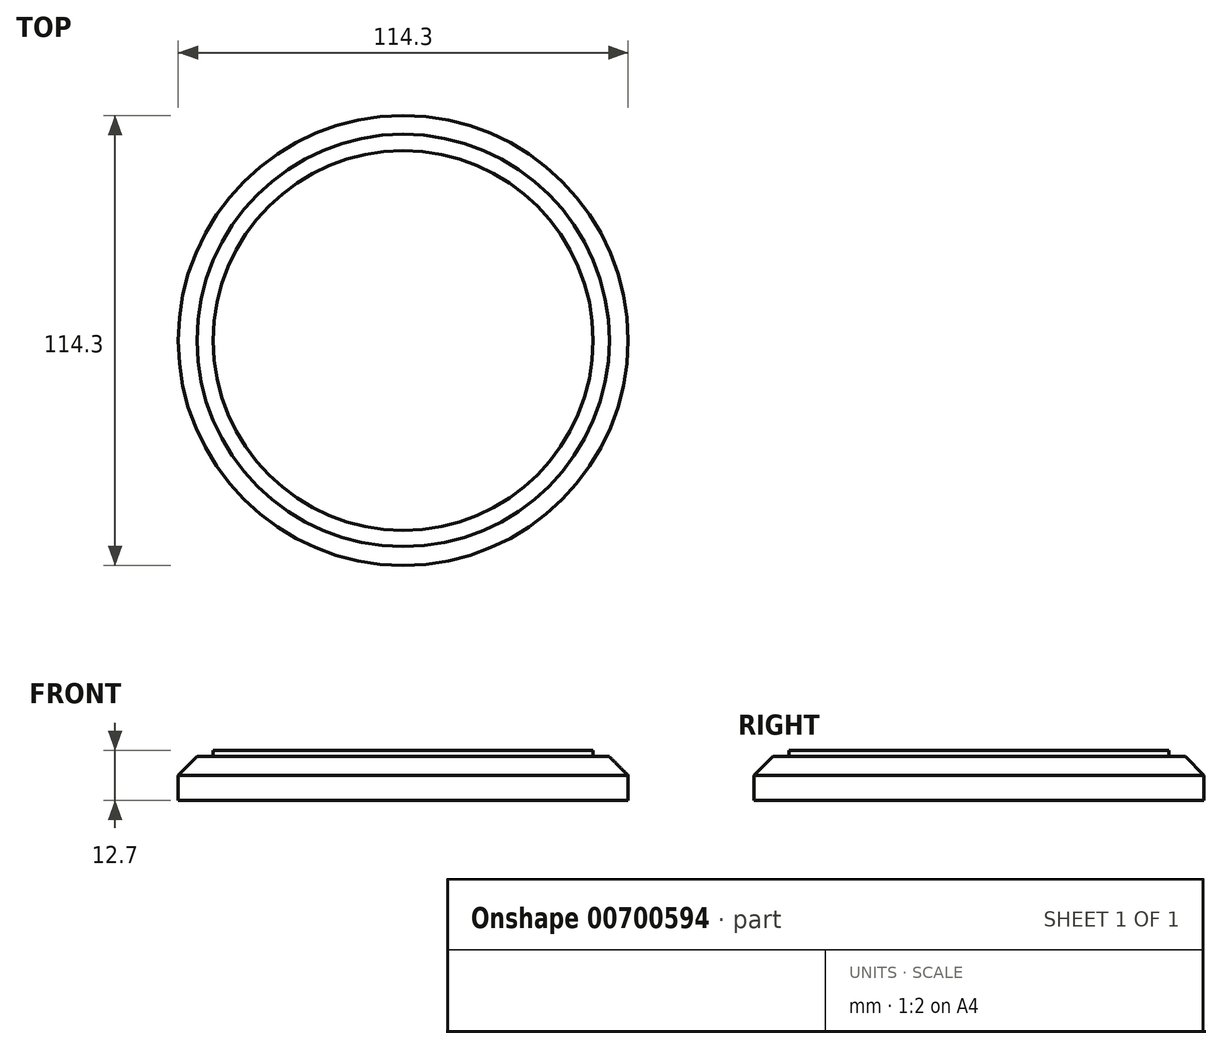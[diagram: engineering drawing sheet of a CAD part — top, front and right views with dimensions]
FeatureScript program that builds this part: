
annotation { "Feature Type Name" : "Feature", "Feature Type Description" : "" }
export const myFeature = defineFeature(function(context is Context, id is Id, definition is map)
    precondition{}
    {
        {
            var Q0;
            Q0=qCreatedBy(makeId("Top.planeOp"),FACE);
            var sketch = newSketch(context, id + "F0", { "sketchPlane" : qUnion([Q0])});
            skCircle(sketch, "E0", {"center": v(0, 0) * mm, "radius": 57.15 * mm});
            skSolve(sketch);
        }
        {
            var Q0;
            Q0 = qSketchRegion(id + "F0", true);
            extrude(context, id + "F1", {"entities" : qUnion([Q0]), "depth" : 12.7 * mm, "offsetDistance" : 25.4 * mm});
        }
        {
            var Q0;
            Q0=makeQuery(id+"F1.opExtrude","CAP_FACE",FACE,{"disambiguationData":[OSD([sQuery(id+"F0.wireOp",EDGE,"E0")])],"isStart":false});
            var sketch = newSketch(context, id + "F2", { "sketchPlane" : qUnion([Q0])});
            skCircle(sketch, "E1", {"center": v(0, 0) * mm, "radius": 48.26 * mm});
            skCircle(sketch, "E2", {"center": v(0, 0) * mm, "radius": 82.07 * mm});
            skSolve(sketch);
        }
        {
            var Q0;
            Q0 = qSketchRegion(id + "F2", true);
            extrude(context, id + "F3", {"entities" : qUnion([Q0]), "operationType" : NewBodyOperationType.REMOVE, "oppositeDirection" : true, "depth" : 1.59 * mm, "offsetDistance" : 25.4 * mm});
        }
        {
            var Q0;
            Q0=makeQuery(id+"F3.boolean.opBoolean","INTERSECT",EDGE,{"derivedFrom":[makeQuery(id+"F1.opExtrude","SWEPT_FACE",FACE,{"disambiguationData":[OSD([sQuery(id+"F0.wireOp",EDGE,"E0")])]}),makeQuery(id+"F3.opExtrude","CAP_FACE",FACE,{"disambiguationData":[OSD([sQuery(id+"F2.wireOp",EDGE,"E1"),sQuery(id+"F2.wireOp",EDGE,"E2")])],"isStart":false})]});
            chamfer(context, id + "F4", {"entities" : qUnion([Q0]), "width" : 4.76 * mm, "tangentPropagation" : true});
        }
    });
